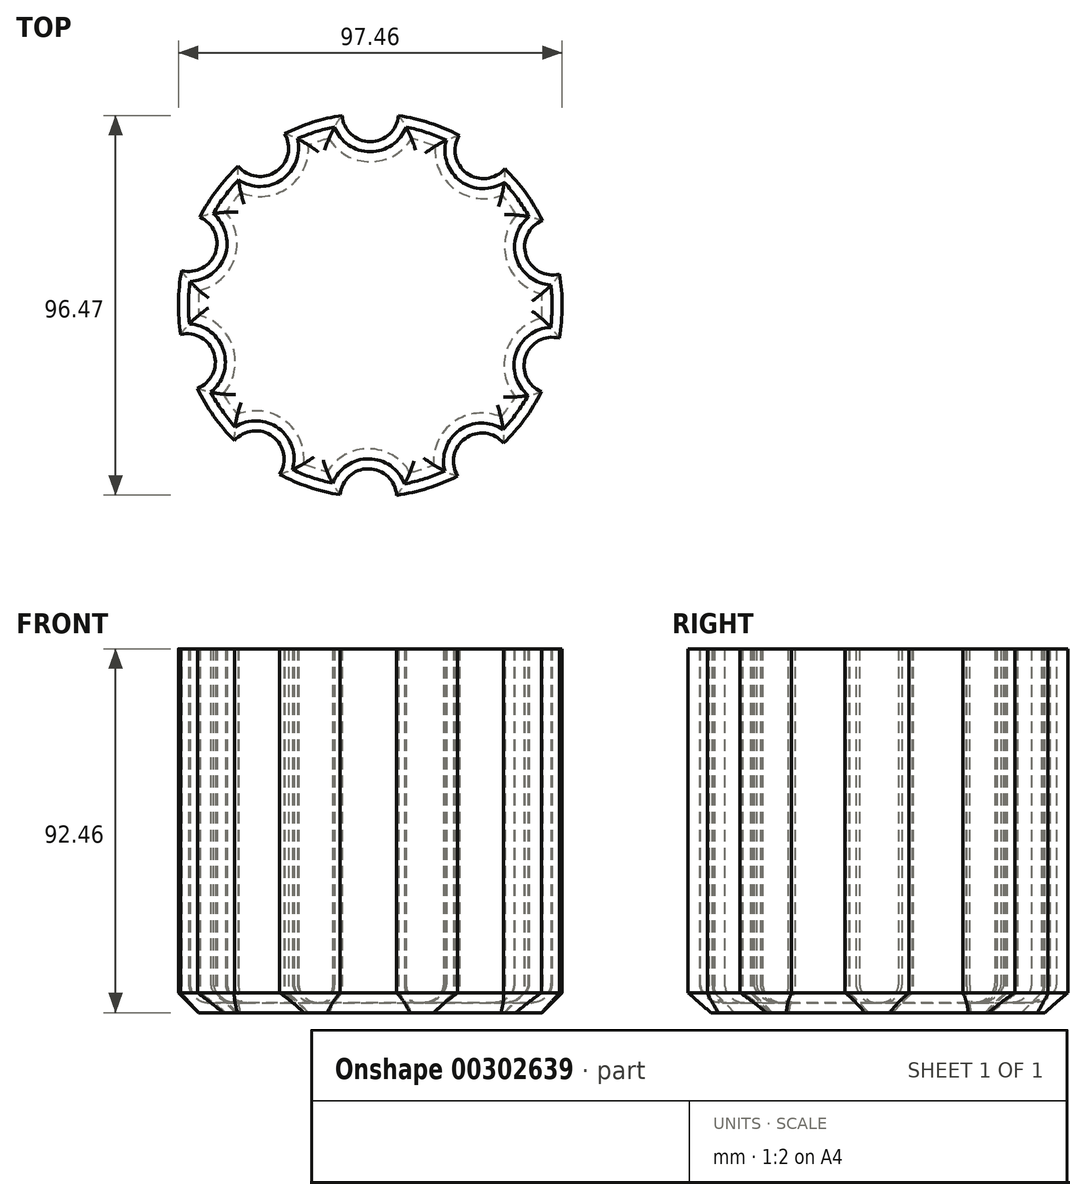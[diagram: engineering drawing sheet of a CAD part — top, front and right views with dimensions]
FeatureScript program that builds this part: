
annotation { "Feature Type Name" : "Feature", "Feature Type Description" : "" }
export const myFeature = defineFeature(function(context is Context, id is Id, definition is map)
    precondition{}
    {
        {
            var Q0;
            Q0=qCreatedBy(makeId("Top.planeOp"),FACE);
            var sketch = newSketch(context, id + "F0", { "sketchPlane" : qUnion([Q0])});
            skCircle(sketch, "E0", {"center": v(0, 0) * mm, "radius": 48.73 * mm});
            skCircle(sketch, "E1", {"center": v(0, 48.73) * mm, "radius": 7.2 * mm});
            skCircle(sketch, "E2.1.0", {"center": v(28.72, 39.37) * mm, "radius": 7.2 * mm});
            skCircle(sketch, "E2.2.0", {"center": v(46.4, 14.88) * mm, "radius": 7.2 * mm});
            skCircle(sketch, "E2.3.0", {"center": v(46.26, -15.33) * mm, "radius": 7.2 * mm});
            skCircle(sketch, "E2.4.0", {"center": v(28.34, -39.65) * mm, "radius": 7.2 * mm});
            skCircle(sketch, "E2.5.0", {"center": v(-0.47, -48.73) * mm, "radius": 7.2 * mm});
            skCircle(sketch, "E2.6.0", {"center": v(-29.1, -39.1) * mm, "radius": 7.2 * mm});
            skCircle(sketch, "E2.7.0", {"center": v(-46.55, -14.43) * mm, "radius": 7.2 * mm});
            skCircle(sketch, "E2.8.0", {"center": v(-46.11, 15.78) * mm, "radius": 7.2 * mm});
            skCircle(sketch, "E2.9.0", {"center": v(-27.95, 39.92) * mm, "radius": 7.2 * mm});
            skLineSegment(sketch, "E2.anchor1", {"start": v(0, 0) * mm, "end": v(0, 48.73) * mm, "construction": true});
            skLineSegment(sketch, "E2.anchor2", {"start": v(0, 0) * mm, "end": v(-27.95, 39.92) * mm, "construction": true});
            skSolve(sketch);
        }
        {
            var Q0;
            {var subQ0=sQuery(id+"F0.wireOp",EDGE,"E2.2.0");var subQ1=sQuery(id+"F0.wireOp",EDGE,"E0");var subQ24=makeQuery(id+"F0.imprint","INTERSECT",VERTEX,{"disambiguationData":[OD(0.0)],"derivedFrom":[subQ1,subQ0]});Q0=makeQuery(id+"F0.imprint","IMPRINT",FACE,{"disambiguationData":[TD([[makeQuery(id+"F0.imprint","IMPRINT",EDGE,{"disambiguationData":[TD([[subQ24,-1.0]])],"derivedFrom":subQ1}),1.0]])]});}
            extrude(context, id + "F1", {"entities" : qUnion([Q0]), "depth" : 92.46 * mm});
        }
        {
            var Q0;
            Q0=makeQuery(id+"F1.opExtrude","CAP_FACE",FACE,{"disambiguationData":[OSD([sQuery(id+"F0.wireOp",EDGE,"E0"),sQuery(id+"F0.wireOp",EDGE,"E1"),sQuery(id+"F0.wireOp",EDGE,"E2.1.0"),sQuery(id+"F0.wireOp",EDGE,"E2.2.0"),sQuery(id+"F0.wireOp",EDGE,"E2.3.0"),sQuery(id+"F0.wireOp",EDGE,"E2.4.0"),sQuery(id+"F0.wireOp",EDGE,"E2.5.0"),sQuery(id+"F0.wireOp",EDGE,"E2.6.0"),sQuery(id+"F0.wireOp",EDGE,"E2.7.0"),sQuery(id+"F0.wireOp",EDGE,"E2.8.0"),sQuery(id+"F0.wireOp",EDGE,"E2.9.0")])],"isStart":false});
            shell(context, id + "F2", {"entities" : qUnion([Q0]), "thickness" : 2.54 * mm});
        }
        {
            var Q0;
            Q0=makeQuery(id+"F2.opShell","OFFSET_FACE",FACE,{"disambiguationData":[OSD([sQuery(id+"F0.wireOp",EDGE,"E0"),sQuery(id+"F0.wireOp",EDGE,"E1"),sQuery(id+"F0.wireOp",EDGE,"E2.1.0"),sQuery(id+"F0.wireOp",EDGE,"E2.2.0"),sQuery(id+"F0.wireOp",EDGE,"E2.3.0"),sQuery(id+"F0.wireOp",EDGE,"E2.4.0"),sQuery(id+"F0.wireOp",EDGE,"E2.5.0"),sQuery(id+"F0.wireOp",EDGE,"E2.6.0"),sQuery(id+"F0.wireOp",EDGE,"E2.7.0"),sQuery(id+"F0.wireOp",EDGE,"E2.8.0"),sQuery(id+"F0.wireOp",EDGE,"E2.9.0")])]});
            fillet(context, id + "F3", {"entities" : qUnion([Q0]), "radius" : 5.08 * mm, "tangentPropagation" : true, "allowEdgeOverflow" : false});
        }
        {
            var Q0;
            Q0=makeQuery(id+"F1.opExtrude","CAP_FACE",FACE,{"disambiguationData":[OSD([sQuery(id+"F0.wireOp",EDGE,"E0"),sQuery(id+"F0.wireOp",EDGE,"E1"),sQuery(id+"F0.wireOp",EDGE,"E2.1.0"),sQuery(id+"F0.wireOp",EDGE,"E2.2.0"),sQuery(id+"F0.wireOp",EDGE,"E2.3.0"),sQuery(id+"F0.wireOp",EDGE,"E2.4.0"),sQuery(id+"F0.wireOp",EDGE,"E2.5.0"),sQuery(id+"F0.wireOp",EDGE,"E2.6.0"),sQuery(id+"F0.wireOp",EDGE,"E2.7.0"),sQuery(id+"F0.wireOp",EDGE,"E2.8.0"),sQuery(id+"F0.wireOp",EDGE,"E2.9.0")])],"isStart":true});
            chamfer(context, id + "F4", {"entities" : qUnion([Q0]), "width" : 5.08 * mm, "tangentPropagation" : true});
        }
    });
